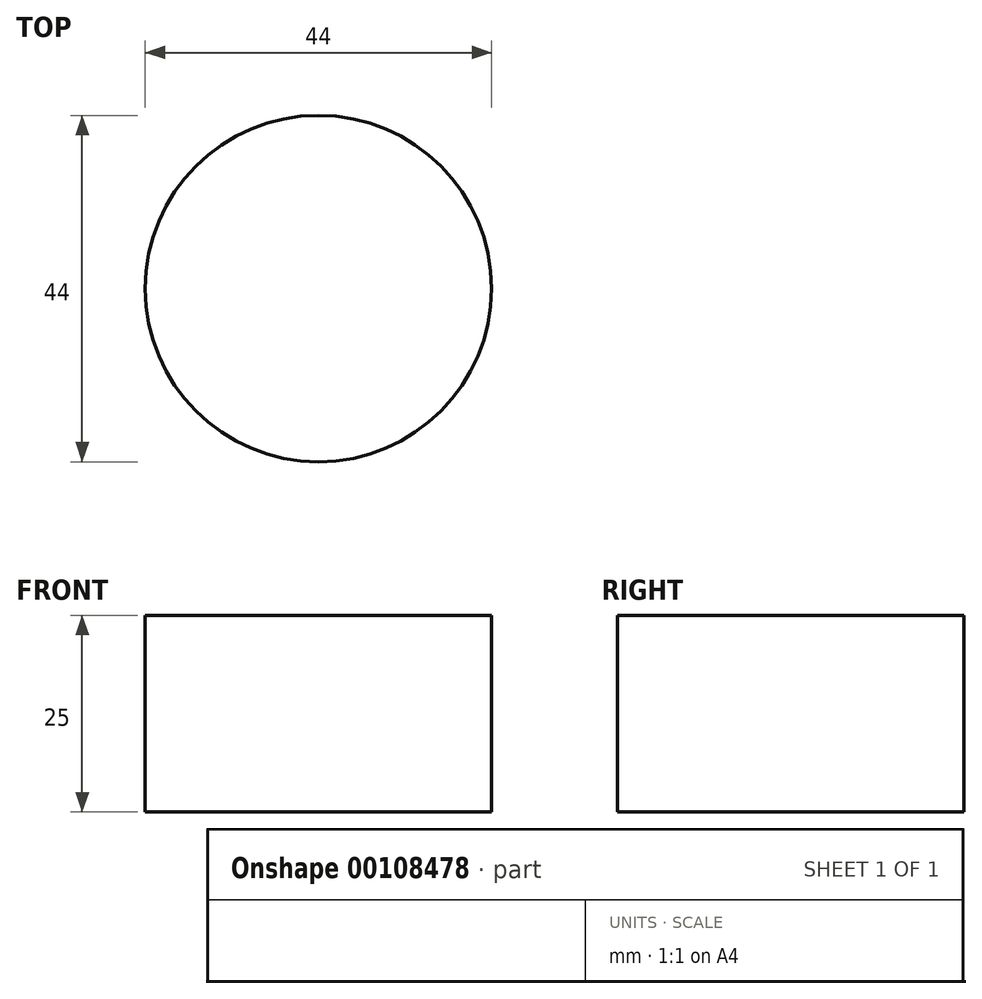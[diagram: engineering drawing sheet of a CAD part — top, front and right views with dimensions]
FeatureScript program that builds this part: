
annotation { "Feature Type Name" : "Feature", "Feature Type Description" : "" }
export const myFeature = defineFeature(function(context is Context, id is Id, definition is map)
    precondition{}
    {
        {
            var Q0;
            Q0=qCreatedBy(makeId("Top.planeOp"),FACE);
            var sketch = newSketch(context, id + "F0", { "sketchPlane" : qUnion([Q0])});
            skCircle(sketch, "E0", {"center": v(0, 0) * mm, "radius": 22 * mm});
            skSolve(sketch);
        }
        {
            var Q0;
            Q0=makeQuery(id+"F0.imprint","IMPRINT",FACE,{"disambiguationData":[TD([[makeQuery(id+"F0.imprint","IMPRINT",EDGE,{"derivedFrom":sQuery(id+"F0.wireOp",EDGE,"E0")}),1.0]])]});
            extrude(context, id + "F1", {"entities" : qUnion([Q0]), "depth" : 25 * mm});
        }
    });
